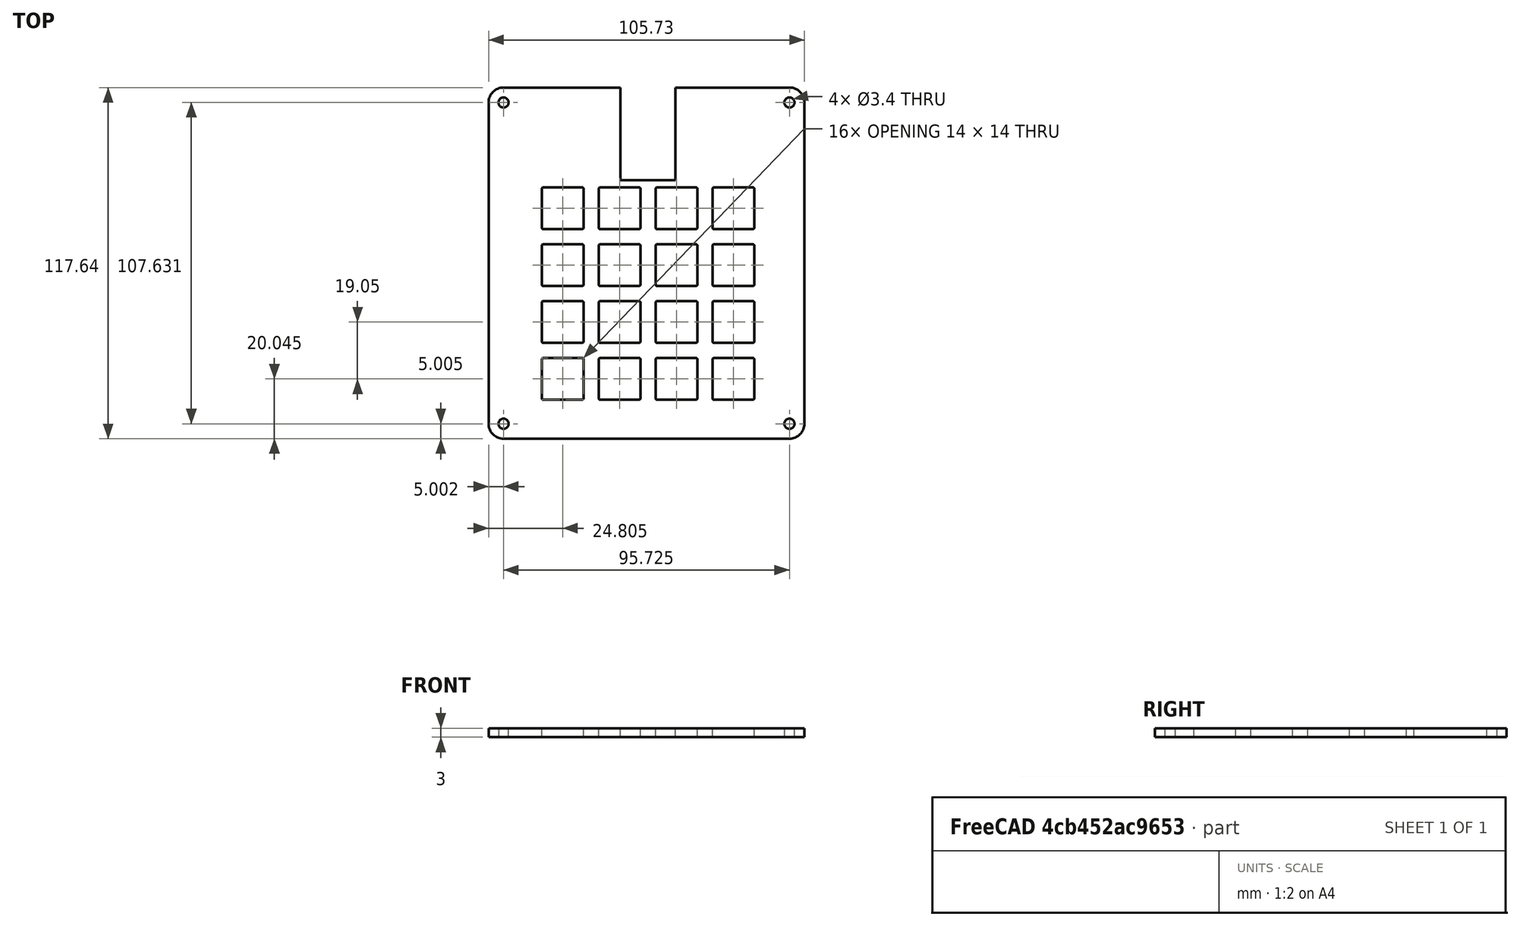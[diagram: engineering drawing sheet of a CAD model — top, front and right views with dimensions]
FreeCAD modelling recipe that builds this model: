
FCSTD DOCUMENT  (FreeCAD 1.0R39109 (Git))
Label: case_top
License: All rights reserved
objects: Sketcher::SketchObject×2, PartDesign::Pad×1, PartDesign::Pocket×1, PartDesign::Body×1
note: 11 computed .brp shape members not serialized (recipe doc carries the construction recipe); baked Part::Feature solids carry a one-line shape summary decoded from their .brp

FEATURE [Sketcher::SketchObject] Sketch001
  ArcFitTolerance = 1e-06
  FullyConstrained = false
  MakeInternals = false
  Placement = pos=(0,23,0) rot=(0,0,1;0rad)
  sketch-geometry (128):
    g0: ArcOfCircle CenterX=73.175 CenterY=-73.175 CenterZ=0 NormalX=0 NormalY=0 NormalZ=1 AngleXU=0 Radius=0.5 StartAngle=4.71239 EndAngle=6.28319
    g1: LineSegment StartX=3.025 StartY=-2.525 StartZ=0 EndX=16.025 EndY=-2.525 EndZ=0
    g2: LineSegment StartX=3.025 StartY=-16.525 StartZ=0 EndX=16.025 EndY=-16.525 EndZ=0
    g3: LineSegment StartX=2.525 StartY=-3.025 StartZ=0 EndX=2.525 EndY=-16.025 EndZ=0
    g4: LineSegment StartX=16.525 StartY=-3.025 StartZ=0 EndX=16.525 EndY=-16.025 EndZ=0
    g5: ArcOfCircle CenterX=3.025 CenterY=-3.025 CenterZ=0 NormalX=0 NormalY=0 NormalZ=1 AngleXU=0 Radius=0.5 StartAngle=1.5708 EndAngle=3.14159
    g6: ArcOfCircle CenterX=16.025 CenterY=-3.025 CenterZ=0 NormalX=0 NormalY=0 NormalZ=1 AngleXU=0 Radius=0.5 StartAngle=0 EndAngle=1.5708
    g7: ArcOfCircle CenterX=3.025 CenterY=-16.025 CenterZ=0 NormalX=0 NormalY=0 NormalZ=1 AngleXU=0 Radius=0.5 StartAngle=3.14159 EndAngle=4.71239
    g8: ArcOfCircle CenterX=16.025 CenterY=-16.025 CenterZ=0 NormalX=0 NormalY=0 NormalZ=1 AngleXU=0 Radius=0.5 StartAngle=4.71239 EndAngle=6.28319
    g9: LineSegment StartX=22.075 StartY=-2.525 StartZ=0 EndX=35.075 EndY=-2.525 EndZ=0
    g10: LineSegment StartX=22.075 StartY=-16.525 StartZ=0 EndX=35.075 EndY=-16.525 EndZ=0
    g11: LineSegment StartX=21.575 StartY=-3.025 StartZ=0 EndX=21.575 EndY=-16.025 EndZ=0
    g12: LineSegment StartX=35.575 StartY=-3.025 StartZ=0 EndX=35.575 EndY=-16.025 EndZ=0
    g13: ArcOfCircle CenterX=22.075 CenterY=-3.025 CenterZ=0 NormalX=0 NormalY=0 NormalZ=1 AngleXU=0 Radius=0.5 StartAngle=1.5708 EndAngle=3.14159
    g14: ArcOfCircle CenterX=35.075 CenterY=-3.025 CenterZ=0 NormalX=0 NormalY=0 NormalZ=1 AngleXU=0 Radius=0.5 StartAngle=0 EndAngle=1.5708
    g15: ArcOfCircle CenterX=22.075 CenterY=-16.025 CenterZ=0 NormalX=0 NormalY=0 NormalZ=1 AngleXU=0 Radius=0.5 StartAngle=3.14159 EndAngle=4.71239
    g16: ArcOfCircle CenterX=35.075 CenterY=-16.025 CenterZ=0 NormalX=0 NormalY=0 NormalZ=1 AngleXU=0 Radius=0.5 StartAngle=4.71239 EndAngle=6.28319
    g17: LineSegment StartX=41.125 StartY=-2.525 StartZ=0 EndX=54.125 EndY=-2.525 EndZ=0
    g18: LineSegment StartX=41.125 StartY=-16.525 StartZ=0 EndX=54.125 EndY=-16.525 EndZ=0
    g19: LineSegment StartX=40.625 StartY=-3.025 StartZ=0 EndX=40.625 EndY=-16.025 EndZ=0
    g20: LineSegment StartX=54.625 StartY=-3.025 StartZ=0 EndX=54.625 EndY=-16.025 EndZ=0
    g21: ArcOfCircle CenterX=41.125 CenterY=-3.025 CenterZ=0 NormalX=0 NormalY=0 NormalZ=1 AngleXU=0 Radius=0.5 StartAngle=1.5708 EndAngle=3.14159
    g22: ArcOfCircle CenterX=54.125 CenterY=-3.025 CenterZ=0 NormalX=0 NormalY=0 NormalZ=1 AngleXU=0 Radius=0.5 StartAngle=0 EndAngle=1.5708
    g23: ArcOfCircle CenterX=41.125 CenterY=-16.025 CenterZ=0 NormalX=0 NormalY=0 NormalZ=1 AngleXU=0 Radius=0.5 StartAngle=3.14159 EndAngle=4.71239
    g24: ArcOfCircle CenterX=54.125 CenterY=-16.025 CenterZ=0 NormalX=0 NormalY=0 NormalZ=1 AngleXU=0 Radius=0.5 StartAngle=4.71239 EndAngle=6.28319
    g25: LineSegment StartX=60.175 StartY=-2.525 StartZ=0 EndX=73.175 EndY=-2.525 EndZ=0
    g26: LineSegment StartX=60.175 StartY=-16.525 StartZ=0 EndX=73.175 EndY=-16.525 EndZ=0
    g27: LineSegment StartX=59.675 StartY=-3.025 StartZ=0 EndX=59.675 EndY=-16.025 EndZ=0
    g28: LineSegment StartX=73.675 StartY=-3.025 StartZ=0 EndX=73.675 EndY=-16.025 EndZ=0
    g29: ArcOfCircle CenterX=60.175 CenterY=-3.025 CenterZ=0 NormalX=0 NormalY=0 NormalZ=1 AngleXU=0 Radius=0.5 StartAngle=1.5708 EndAngle=3.14159
    g30: ArcOfCircle CenterX=73.175 CenterY=-3.025 CenterZ=0 NormalX=0 NormalY=0 NormalZ=1 AngleXU=0 Radius=0.5 StartAngle=0 EndAngle=1.5708
    g31: ArcOfCircle CenterX=60.175 CenterY=-16.025 CenterZ=0 NormalX=0 NormalY=0 NormalZ=1 AngleXU=0 Radius=0.5 StartAngle=3.14159 EndAngle=4.71239
    g32: ArcOfCircle CenterX=73.175 CenterY=-16.025 CenterZ=0 NormalX=0 NormalY=0 NormalZ=1 AngleXU=0 Radius=0.5 StartAngle=4.71239 EndAngle=6.28319
    g33: LineSegment StartX=3.025 StartY=-21.575 StartZ=0 EndX=16.025 EndY=-21.575 EndZ=0
    g34: LineSegment StartX=3.025 StartY=-35.575 StartZ=0 EndX=16.025 EndY=-35.575 EndZ=0
    g35: LineSegment StartX=2.525 StartY=-22.075 StartZ=0 EndX=2.525 EndY=-35.075 EndZ=0
    g36: LineSegment StartX=16.525 StartY=-22.075 StartZ=0 EndX=16.525 EndY=-35.075 EndZ=0
    g37: ArcOfCircle CenterX=3.025 CenterY=-22.075 CenterZ=0 NormalX=0 NormalY=0 NormalZ=1 AngleXU=0 Radius=0.5 StartAngle=1.5708 EndAngle=3.14159
    g38: ArcOfCircle CenterX=16.025 CenterY=-22.075 CenterZ=0 NormalX=0 NormalY=0 NormalZ=1 AngleXU=0 Radius=0.5 StartAngle=0 EndAngle=1.5708
    g39: ArcOfCircle CenterX=3.025 CenterY=-35.075 CenterZ=0 NormalX=0 NormalY=0 NormalZ=1 AngleXU=0 Radius=0.5 StartAngle=3.14159 EndAngle=4.71239
    g40: ArcOfCircle CenterX=16.025 CenterY=-35.075 CenterZ=0 NormalX=0 NormalY=0 NormalZ=1 AngleXU=0 Radius=0.5 StartAngle=4.71239 EndAngle=6.28319
    g41: LineSegment StartX=22.075 StartY=-21.575 StartZ=0 EndX=35.075 EndY=-21.575 EndZ=0
    g42: LineSegment StartX=22.075 StartY=-35.575 StartZ=0 EndX=35.075 EndY=-35.575 EndZ=0
    g43: LineSegment StartX=21.575 StartY=-22.075 StartZ=0 EndX=21.575 EndY=-35.075 EndZ=0
    g44: LineSegment StartX=35.575 StartY=-22.075 StartZ=0 EndX=35.575 EndY=-35.075 EndZ=0
    g45: ArcOfCircle CenterX=22.075 CenterY=-22.075 CenterZ=0 NormalX=0 NormalY=0 NormalZ=1 AngleXU=0 Radius=0.5 StartAngle=1.5708 EndAngle=3.14159
    g46: ArcOfCircle CenterX=35.075 CenterY=-22.075 CenterZ=0 NormalX=0 NormalY=0 NormalZ=1 AngleXU=0 Radius=0.5 StartAngle=0 EndAngle=1.5708
    g47: ArcOfCircle CenterX=22.075 CenterY=-35.075 CenterZ=0 NormalX=0 NormalY=0 NormalZ=1 AngleXU=0 Radius=0.5 StartAngle=3.14159 EndAngle=4.71239
    g48: ArcOfCircle CenterX=35.075 CenterY=-35.075 CenterZ=0 NormalX=0 NormalY=0 NormalZ=1 AngleXU=0 Radius=0.5 StartAngle=4.71239 EndAngle=6.28319
    g49: LineSegment StartX=41.125 StartY=-21.575 StartZ=0 EndX=54.125 EndY=-21.575 EndZ=0
    g50: LineSegment StartX=41.125 StartY=-35.575 StartZ=0 EndX=54.125 EndY=-35.575 EndZ=0
    g51: LineSegment StartX=40.625 StartY=-22.075 StartZ=0 EndX=40.625 EndY=-35.075 EndZ=0
    g52: LineSegment StartX=54.625 StartY=-22.075 StartZ=0 EndX=54.625 EndY=-35.075 EndZ=0
    g53: ArcOfCircle CenterX=41.125 CenterY=-22.075 CenterZ=0 NormalX=0 NormalY=0 NormalZ=1 AngleXU=0 Radius=0.5 StartAngle=1.5708 EndAngle=3.14159
    g54: ArcOfCircle CenterX=54.125 CenterY=-22.075 CenterZ=0 NormalX=0 NormalY=0 NormalZ=1 AngleXU=0 Radius=0.5 StartAngle=0 EndAngle=1.5708
    g55: ArcOfCircle CenterX=41.125 CenterY=-35.075 CenterZ=0 NormalX=0 NormalY=0 NormalZ=1 AngleXU=0 Radius=0.5 StartAngle=3.14159 EndAngle=4.71239
    g56: ArcOfCircle CenterX=54.125 CenterY=-35.075 CenterZ=0 NormalX=0 NormalY=0 NormalZ=1 AngleXU=0 Radius=0.5 StartAngle=4.71239 EndAngle=6.28319
    g57: LineSegment StartX=60.175 StartY=-21.575 StartZ=0 EndX=73.175 EndY=-21.575 EndZ=0
    g58: LineSegment StartX=60.175 StartY=-35.575 StartZ=0 EndX=73.175 EndY=-35.575 EndZ=0
    g59: LineSegment StartX=59.675 StartY=-22.075 StartZ=0 EndX=59.675 EndY=-35.075 EndZ=0
    g60: LineSegment StartX=73.675 StartY=-22.075 StartZ=0 EndX=73.675 EndY=-35.075 EndZ=0
    g61: ArcOfCircle CenterX=60.175 CenterY=-22.075 CenterZ=0 NormalX=0 NormalY=0 NormalZ=1 AngleXU=0 Radius=0.5 StartAngle=1.5708 EndAngle=3.14159
    g62: ArcOfCircle CenterX=73.175 CenterY=-22.075 CenterZ=0 NormalX=0 NormalY=0 NormalZ=1 AngleXU=0 Radius=0.5 StartAngle=0 EndAngle=1.5708
    g63: ArcOfCircle CenterX=60.175 CenterY=-35.075 CenterZ=0 NormalX=0 NormalY=0 NormalZ=1 AngleXU=0 Radius=0.5 StartAngle=3.14159 EndAngle=4.71239
    g64: ArcOfCircle CenterX=73.175 CenterY=-35.075 CenterZ=0 NormalX=0 NormalY=0 NormalZ=1 AngleXU=0 Radius=0.5 StartAngle=4.71239 EndAngle=6.28319
    g65: LineSegment StartX=3.025 StartY=-40.625 StartZ=0 EndX=16.025 EndY=-40.625 EndZ=0
    g66: LineSegment StartX=3.025 StartY=-54.625 StartZ=0 EndX=16.025 EndY=-54.625 EndZ=0
    g67: LineSegment StartX=2.525 StartY=-41.125 StartZ=0 EndX=2.525 EndY=-54.125 EndZ=0
    g68: LineSegment StartX=16.525 StartY=-41.125 StartZ=0 EndX=16.525 EndY=-54.125 EndZ=0
    g69: ArcOfCircle CenterX=3.025 CenterY=-41.125 CenterZ=0 NormalX=0 NormalY=0 NormalZ=1 AngleXU=0 Radius=0.5 StartAngle=1.5708 EndAngle=3.14159
    g70: ArcOfCircle CenterX=16.025 CenterY=-41.125 CenterZ=0 NormalX=0 NormalY=0 NormalZ=1 AngleXU=0 Radius=0.5 StartAngle=0 EndAngle=1.5708
    g71: ArcOfCircle CenterX=3.025 CenterY=-54.125 CenterZ=0 NormalX=0 NormalY=0 NormalZ=1 AngleXU=0 Radius=0.5 StartAngle=3.14159 EndAngle=4.71239
    g72: ArcOfCircle CenterX=16.025 CenterY=-54.125 CenterZ=0 NormalX=0 NormalY=0 NormalZ=1 AngleXU=0 Radius=0.5 StartAngle=4.71239 EndAngle=6.28319
    g73: LineSegment StartX=22.075 StartY=-40.625 StartZ=0 EndX=35.075 EndY=-40.625 EndZ=0
    g74: LineSegment StartX=22.075 StartY=-54.625 StartZ=0 EndX=35.075 EndY=-54.625 EndZ=0
    g75: LineSegment StartX=21.575 StartY=-41.125 StartZ=0 EndX=21.575 EndY=-54.125 EndZ=0
    g76: LineSegment StartX=35.575 StartY=-41.125 StartZ=0 EndX=35.575 EndY=-54.125 EndZ=0
    g77: ArcOfCircle CenterX=22.075 CenterY=-41.125 CenterZ=0 NormalX=0 NormalY=0 NormalZ=1 AngleXU=0 Radius=0.5 StartAngle=1.5708 EndAngle=3.14159
    g78: ArcOfCircle CenterX=35.075 CenterY=-41.125 CenterZ=0 NormalX=0 NormalY=0 NormalZ=1 AngleXU=0 Radius=0.5 StartAngle=0 EndAngle=1.5708
    g79: ArcOfCircle CenterX=22.075 CenterY=-54.125 CenterZ=0 NormalX=0 NormalY=0 NormalZ=1 AngleXU=0 Radius=0.5 StartAngle=3.14159 EndAngle=4.71239
    g80: ArcOfCircle CenterX=35.075 CenterY=-54.125 CenterZ=0 NormalX=0 NormalY=0 NormalZ=1 AngleXU=0 Radius=0.5 StartAngle=4.71239 EndAngle=6.28319
    g81: LineSegment StartX=41.125 StartY=-40.625 StartZ=0 EndX=54.125 EndY=-40.625 EndZ=0
    g82: LineSegment StartX=41.125 StartY=-54.625 StartZ=0 EndX=54.125 EndY=-54.625 EndZ=0
    g83: LineSegment StartX=40.625 StartY=-41.125 StartZ=0 EndX=40.625 EndY=-54.125 EndZ=0
    g84: LineSegment StartX=54.625 StartY=-41.125 StartZ=0 EndX=54.625 EndY=-54.125 EndZ=0
    g85: ArcOfCircle CenterX=41.125 CenterY=-41.125 CenterZ=0 NormalX=0 NormalY=0 NormalZ=1 AngleXU=0 Radius=0.5 StartAngle=1.5708 EndAngle=3.14159
    g86: ArcOfCircle CenterX=54.125 CenterY=-41.125 CenterZ=0 NormalX=0 NormalY=0 NormalZ=1 AngleXU=0 Radius=0.5 StartAngle=0 EndAngle=1.5708
    g87: ArcOfCircle CenterX=41.125 CenterY=-54.125 CenterZ=0 NormalX=0 NormalY=0 NormalZ=1 AngleXU=0 Radius=0.5 StartAngle=3.14159 EndAngle=4.71239
    g88: ArcOfCircle CenterX=54.125 CenterY=-54.125 CenterZ=0 NormalX=0 NormalY=0 NormalZ=1 AngleXU=0 Radius=0.5 StartAngle=4.71239 EndAngle=6.28319
    g89: LineSegment StartX=60.175 StartY=-40.625 StartZ=0 EndX=73.175 EndY=-40.625 EndZ=0
    g90: LineSegment StartX=60.175 StartY=-54.625 StartZ=0 EndX=73.175 EndY=-54.625 EndZ=0
    g91: LineSegment StartX=59.675 StartY=-41.125 StartZ=0 EndX=59.675 EndY=-54.125 EndZ=0
    g92: LineSegment StartX=73.675 StartY=-41.125 StartZ=0 EndX=73.675 EndY=-54.125 EndZ=0
    g93: ArcOfCircle CenterX=60.175 CenterY=-41.125 CenterZ=0 NormalX=0 NormalY=0 NormalZ=1 AngleXU=0 Radius=0.5 StartAngle=1.5708 EndAngle=3.14159
    g94: ArcOfCircle CenterX=73.175 CenterY=-41.125 CenterZ=0 NormalX=0 NormalY=0 NormalZ=1 AngleXU=0 Radius=0.5 StartAngle=0 EndAngle=1.5708
    g95: ArcOfCircle CenterX=60.175 CenterY=-54.125 CenterZ=0 NormalX=0 NormalY=0 NormalZ=1 AngleXU=0 Radius=0.5 StartAngle=3.14159 EndAngle=4.71239
    g96: ArcOfCircle CenterX=73.175 CenterY=-54.125 CenterZ=0 NormalX=0 NormalY=0 NormalZ=1 AngleXU=0 Radius=0.5 StartAngle=4.71239 EndAngle=6.28319
    g97: LineSegment StartX=3.025 StartY=-59.675 StartZ=0 EndX=16.025 EndY=-59.675 EndZ=0
    g98: LineSegment StartX=3.025 StartY=-73.675 StartZ=0 EndX=16.025 EndY=-73.675 EndZ=0
    g99: LineSegment StartX=2.525 StartY=-60.175 StartZ=0 EndX=2.525 EndY=-73.175 EndZ=0
    g100: LineSegment StartX=16.525 StartY=-60.175 StartZ=0 EndX=16.525 EndY=-73.175 EndZ=0
    g101: ArcOfCircle CenterX=3.025 CenterY=-60.175 CenterZ=0 NormalX=0 NormalY=0 NormalZ=1 AngleXU=0 Radius=0.5 StartAngle=1.5708 EndAngle=3.14159
    g102: ArcOfCircle CenterX=16.025 CenterY=-60.175 CenterZ=0 NormalX=0 NormalY=0 NormalZ=1 AngleXU=0 Radius=0.5 StartAngle=0 EndAngle=1.5708
    g103: ArcOfCircle CenterX=3.025 CenterY=-73.175 CenterZ=0 NormalX=0 NormalY=0 NormalZ=1 AngleXU=0 Radius=0.5 StartAngle=3.14159 EndAngle=4.71239
    g104: ArcOfCircle CenterX=16.025 CenterY=-73.175 CenterZ=0 NormalX=0 NormalY=0 NormalZ=1 AngleXU=0 Radius=0.5 StartAngle=4.71239 EndAngle=6.28319
    g105: LineSegment StartX=22.075 StartY=-59.675 StartZ=0 EndX=35.075 EndY=-59.675 EndZ=0
    g106: LineSegment StartX=22.075 StartY=-73.675 StartZ=0 EndX=35.075 EndY=-73.675 EndZ=0
    g107: LineSegment StartX=21.575 StartY=-60.175 StartZ=0 EndX=21.575 EndY=-73.175 EndZ=0
    g108: LineSegment StartX=35.575 StartY=-60.175 StartZ=0 EndX=35.575 EndY=-73.175 EndZ=0
    g109: ArcOfCircle CenterX=22.075 CenterY=-60.175 CenterZ=0 NormalX=0 NormalY=0 NormalZ=1 AngleXU=0 Radius=0.5 StartAngle=1.5708 EndAngle=3.14159
    g110: ArcOfCircle CenterX=35.075 CenterY=-60.175 CenterZ=0 NormalX=0 NormalY=0 NormalZ=1 AngleXU=0 Radius=0.5 StartAngle=0 EndAngle=1.5708
    g111: ArcOfCircle CenterX=22.075 CenterY=-73.175 CenterZ=0 NormalX=0 NormalY=0 NormalZ=1 AngleXU=0 Radius=0.5 StartAngle=3.14159 EndAngle=4.71239
    g112: ArcOfCircle CenterX=35.075 CenterY=-73.175 CenterZ=0 NormalX=0 NormalY=0 NormalZ=1 AngleXU=0 Radius=0.5 StartAngle=4.71239 EndAngle=6.28319
    g113: LineSegment StartX=41.125 StartY=-59.675 StartZ=0 EndX=54.125 EndY=-59.675 EndZ=0
    g114: LineSegment StartX=41.125 StartY=-73.675 StartZ=0 EndX=54.125 EndY=-73.675 EndZ=0
    g115: LineSegment StartX=40.625 StartY=-60.175 StartZ=0 EndX=40.625 EndY=-73.175 EndZ=0
    g116: LineSegment StartX=54.625 StartY=-60.175 StartZ=0 EndX=54.625 EndY=-73.175 EndZ=0
    g117: ArcOfCircle CenterX=41.125 CenterY=-60.175 CenterZ=0 NormalX=0 NormalY=0 NormalZ=1 AngleXU=0 Radius=0.5 StartAngle=1.5708 EndAngle=3.14159
    g118: ArcOfCircle CenterX=54.125 CenterY=-60.175 CenterZ=0 NormalX=0 NormalY=0 NormalZ=1 AngleXU=0 Radius=0.5 StartAngle=0 EndAngle=1.5708
    g119: ArcOfCircle CenterX=41.125 CenterY=-73.175 CenterZ=0 NormalX=0 NormalY=0 NormalZ=1 AngleXU=0 Radius=0.5 StartAngle=3.14159 EndAngle=4.71239
    g120: ArcOfCircle CenterX=54.125 CenterY=-73.175 CenterZ=0 NormalX=0 NormalY=0 NormalZ=1 AngleXU=0 Radius=0.5 StartAngle=4.71239 EndAngle=6.28319
    g121: LineSegment StartX=60.175 StartY=-59.675 StartZ=0 EndX=73.175 EndY=-59.675 EndZ=0
    g122: LineSegment StartX=60.175 StartY=-73.675 StartZ=0 EndX=73.175 EndY=-73.675 EndZ=0
    g123: LineSegment StartX=59.675 StartY=-60.175 StartZ=0 EndX=59.675 EndY=-73.175 EndZ=0
    g124: LineSegment StartX=73.675 StartY=-60.175 StartZ=0 EndX=73.675 EndY=-73.175 EndZ=0
    g125: ArcOfCircle CenterX=60.175 CenterY=-60.175 CenterZ=0 NormalX=0 NormalY=0 NormalZ=1 AngleXU=0 Radius=0.5 StartAngle=1.5708 EndAngle=3.14159
    g126: ArcOfCircle CenterX=73.175 CenterY=-60.175 CenterZ=0 NormalX=0 NormalY=0 NormalZ=1 AngleXU=0 Radius=0.5 StartAngle=0 EndAngle=1.5708
    g127: ArcOfCircle CenterX=60.175 CenterY=-73.175 CenterZ=0 NormalX=0 NormalY=0 NormalZ=1 AngleXU=0 Radius=0.5 StartAngle=3.14159 EndAngle=4.71239
FEATURE [Sketcher::SketchObject] Sketch
  ArcFitTolerance = 1e-06
  AttachmentSupport = -> [XY_Plane]
  ExternalGeometry = -> [Sketch001]
  FullyConstrained = false
  MakeInternals = false
  MapMode = 5
  sketch-geometry (18):
    g0: LineSegment StartX=-15.278 StartY=48.916 StartZ=0 EndX=-15.278 EndY=-58.715 EndZ=0
    g1: LineSegment StartX=-10.278 StartY=-63.715 StartZ=0 EndX=85.447 EndY=-63.715 EndZ=0
    g2: LineSegment StartX=90.447 StartY=-58.715 StartZ=0 EndX=90.447 EndY=48.916 EndZ=0
    g3: LineSegment StartX=85.447 StartY=53.916 StartZ=0 EndX=47.3168 EndY=53.916 EndZ=0
    g4: ArcOfCircle CenterX=-10.278 CenterY=48.916 CenterZ=0 NormalX=0 NormalY=0 NormalZ=1 AngleXU=0 Radius=5 StartAngle=1.5708 EndAngle=3.14159
    g5: ArcOfCircle CenterX=-10.278 CenterY=-58.715 CenterZ=0 NormalX=0 NormalY=0 NormalZ=1 AngleXU=0 Radius=5 StartAngle=3.14159 EndAngle=4.71239
    g6: ArcOfCircle CenterX=85.447 CenterY=-58.715 CenterZ=0 NormalX=0 NormalY=0 NormalZ=1 AngleXU=0 Radius=5 StartAngle=4.71239 EndAngle=6.28319
    g7: ArcOfCircle CenterX=85.447 CenterY=48.916 CenterZ=0 NormalX=0 NormalY=0 NormalZ=1 AngleXU=0 Radius=5 StartAngle=2e-16 EndAngle=1.5708
    g8: GeomPoint [constr] X=-15.278 Y=53.916 Z=0
    g9: GeomPoint [constr] X=90.447 Y=-63.715 Z=0
    g10: Circle CenterX=-10.278 CenterY=-58.715 CenterZ=0 NormalX=0 NormalY=0 NormalZ=1 AngleXU=0 Radius=1.7
    g11: Circle CenterX=-10.278 CenterY=48.916 CenterZ=0 NormalX=0 NormalY=0 NormalZ=1 AngleXU=0 Radius=1.7
    g12: Circle CenterX=85.447 CenterY=48.916 CenterZ=0 NormalX=0 NormalY=0 NormalZ=1 AngleXU=0 Radius=1.7
    g13: Circle CenterX=85.447 CenterY=-58.715 CenterZ=0 NormalX=0 NormalY=0 NormalZ=1 AngleXU=0 Radius=1.7
    g14: LineSegment StartX=28.8168 StartY=53.916 StartZ=0 EndX=28.8168 EndY=22.916 EndZ=0
    g15: LineSegment StartX=28.8168 StartY=22.916 StartZ=0 EndX=47.3168 EndY=22.916 EndZ=0
    g16: LineSegment StartX=47.3168 StartY=22.916 StartZ=0 EndX=47.3168 EndY=53.916 EndZ=0
    g17: LineSegment StartX=28.8168 StartY=53.916 StartZ=0 EndX=-10.278 EndY=53.916 EndZ=0
  constraints (46):
    c: Tangent(g0,g4) = -1.5708
    c: Tangent(g0,g5) = -1.5708
    c: Tangent(g1,g5) = -1.5708
    c: Tangent(g1,g6) = -1.5708
    c: Tangent(g2,g6) = -1.5708
    c: Tangent(g2,g7) = -1.5708
    c: Tangent(g3,g7) = -1.5708
    c: Coincident(g17,g4) = -1.5708
    c: Vertical(g0)
    c: Vertical(g2)
    c: Horizontal(g1)
    c: Horizontal(g3)
    c: Equal(g4,g5)
    c: Equal(g5,g6)
    c: Equal(g6,g7)
    c: PointOnObject(g8,g0)
    c: PointOnObject(g8,g17)
    c: PointOnObject(g9,g1)
    c: PointOnObject(g9,g2)
    c: Radius(g4) = 5
    c: DistanceX(g17,g3) = 95.725
    c: DistanceY(g0,g0) = 107.631
    c: Distance(g1,g-4) = 13.04
    c: Distance(g0,g-3) = 17.803
    c: Diameter(g10) = 3.4
    c: Distance(g10,g0) = 5
    c: Distance(g10,g1) = 5
    c: Diameter(g11) = 3.4
    c: Distance(g11,g0) = 5
    c: Distance(g11,g3) = 5
    c: Diameter(g12) = 3.4
    c: Distance(g12,g2) = 5
    c: Distance(g12,g3) = 5
    c: Diameter(g13) = 3.4
    c: Distance(g13,g1) = 5
    c: Distance(g13,g2) = 5
    c: Coincident(g14,g15)
    c: Coincident(g15,g16)
    c: Vertical(g14)
    c: Vertical(g16)
    c: Horizontal(g15)
    c: PointOnObject(g14,g17)
    c: DistanceX(g15,g15) = 18.5
    c: DistanceY(g16,g16) = 31
    c: PointOnObject(g3,g16)
    c: PointOnObject(g17,g14)
FEATURE [PartDesign::Pad] Pad
  Direction = (0,0,1)
  Length = 3
  Length2 = 10
  Profile = -> Sketch
  ReferenceAxis = -> Sketch [N_Axis]
  Refine = true
  Suppressed = false
  Type = 0
FEATURE [PartDesign::Pocket] Pocket
  BaseFeature = -> Pad
  Direction = (0,0,-1)
  Length = 10
  Length2 = 5
  Profile = -> Sketch001
  ReferenceAxis = -> Sketch001 [N_Axis]
  Refine = true
  Reversed = true
  Suppressed = false
  Type = 0
FEATURE [PartDesign::Body] Body
  AllowCompound = false
  Group = -> [Sketch,Sketch001,Pad,Pocket]
  Origin = -> Origin
  Tip = -> Pocket
